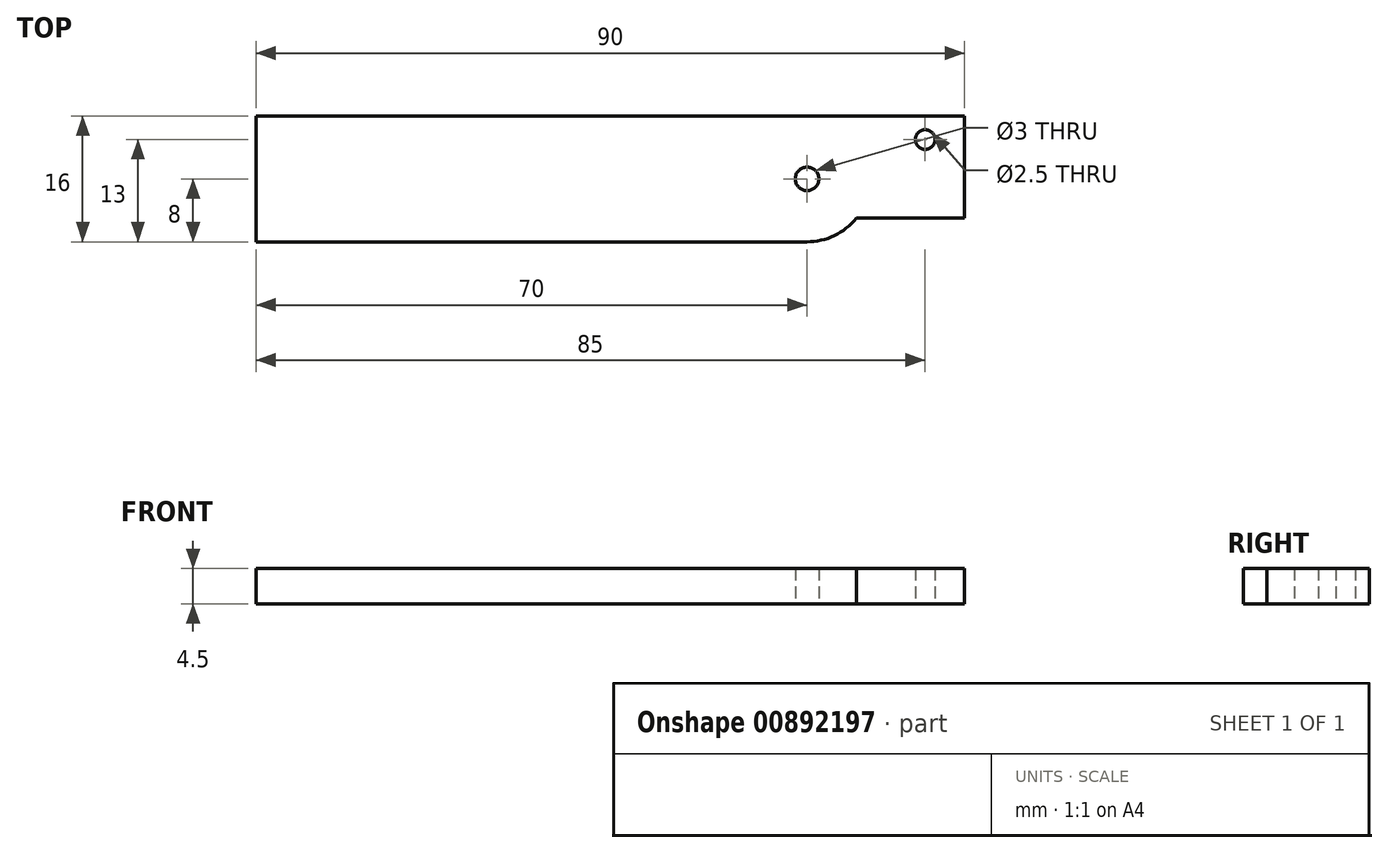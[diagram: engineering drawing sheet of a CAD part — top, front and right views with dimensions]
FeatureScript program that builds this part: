
annotation { "Feature Type Name" : "Feature", "Feature Type Description" : "" }
export const myFeature = defineFeature(function(context is Context, id is Id, definition is map)
    precondition{}
    {
        {
            var Q0;
            Q0=qCreatedBy(makeId("Top.planeOp"),FACE);
            var sketch = newSketch(context, id + "F0", { "sketchPlane" : qUnion([Q0])});
            skLineSegment(sketch, "E0.bottom", {"start": v(35, 8) * mm, "end": v(-35, 8) * mm});
            skLineSegment(sketch, "E0.top", {"start": v(35, -8) * mm, "end": v(-35, -8) * mm});
            skLineSegment(sketch, "E0.left", {"start": v(35, 8) * mm, "end": v(35, -8) * mm});
            skLineSegment(sketch, "E0.right", {"start": v(-35, 8) * mm, "end": v(-35, -8) * mm});
            skPoint(sketch, "E0.middle", {"position": v(0, 0) * mm});
            skArc(sketch, "E1", {"start": v(35, 8) * mm, "mid": v(43, 0) * mm, "end": v(35, -8) * mm});
            skPoint(sketch, "E2", {"position": v(35, -5) * mm});
            skLineSegment(sketch, "E3.bottom", {"start": v(35, -5) * mm, "end": v(55, -5) * mm});
            skLineSegment(sketch, "E3.top", {"start": v(35, 8) * mm, "end": v(55, 8) * mm});
            skLineSegment(sketch, "E3.left", {"start": v(35, -5) * mm, "end": v(35, 8) * mm});
            skLineSegment(sketch, "E3.right", {"start": v(55, -5) * mm, "end": v(55, 8) * mm});
            skPoint(sketch, "E4", {"position": v(50, 5) * mm});
            skSolve(sketch);
        }
        {
            var Q0;
            {var subQ4=sQuery(id+"F0.wireOp",EDGE,"E0.bottom");Q0=makeQuery(id+"F0.imprint","IMPRINT",FACE,{"disambiguationData":[TD([[makeQuery(id+"F0.imprint","IMPRINT",EDGE,{"derivedFrom":subQ4}),1.0]])]});}
            var Q1;
            {var subQ0=sQuery(id+"F0.wireOp",EDGE,"E1");var subQ3=sQuery(id+"F0.wireOp",EDGE,"E3.bottom");var subQ5=makeQuery(id+"F0.imprint","INTERSECT",VERTEX,{"derivedFrom":[subQ0,subQ3]});Q1=makeQuery(id+"F0.imprint","IMPRINT",FACE,{"disambiguationData":[TD([[makeQuery(id+"F0.imprint","IMPRINT",EDGE,{"disambiguationData":[TD([[subQ5,1.0]])],"derivedFrom":subQ3}),-1.0]])]});}
            var Q2;
            {var subQ0=sQuery(id+"F0.wireOp",EDGE,"E1");var subQ3=sQuery(id+"F0.wireOp",EDGE,"E3.bottom");var subQ5=makeQuery(id+"F0.imprint","INTERSECT",VERTEX,{"derivedFrom":[subQ0,subQ3]});Q2=makeQuery(id+"F0.imprint","IMPRINT",FACE,{"disambiguationData":[TD([[makeQuery(id+"F0.imprint","IMPRINT",EDGE,{"disambiguationData":[TD([[subQ5,1.0]])],"derivedFrom":subQ3}),1.0]])]});}
            var Q3;
            {var subQ0=sQuery(id+"F0.wireOp",EDGE,"E3.top");Q3=makeQuery(id+"F0.imprint","IMPRINT",FACE,{"disambiguationData":[TD([[makeQuery(id+"F0.imprint","IMPRINT",EDGE,{"derivedFrom":subQ0}),-1.0]])]});}
            extrude(context, id + "F1", {"entities" : qUnion([Q0, Q1, Q2, Q3]), "depth" : 4.5 * mm, "offsetDistance" : 25.4 * mm});
        }
        {
            var Q0;
            Q0=sQuery(id+"F0.wireOp",VERTEX,"E1.center");
            var Q1;
            Q1=makeQuery(id+"F1.opExtrude","SWEPT_BODY",BODY,{"disambiguationData":[OSD([sQuery(id+"F0.wireOp",EDGE,"E0.bottom"),sQuery(id+"F0.wireOp",EDGE,"E0.top"),sQuery(id+"F0.wireOp",EDGE,"E0.right"),sQuery(id+"F0.wireOp",EDGE,"E1"),sQuery(id+"F0.wireOp",EDGE,"E3.bottom"),sQuery(id+"F0.wireOp",EDGE,"E3.top"),sQuery(id+"F0.wireOp",EDGE,"E3.right")])]});
            hole(context, id + "F2", {"style" : HoleStyle.SIMPLE, "endStyle" : HoleEndStyle.BLIND, "oppositeDirection" : true, "holeDiameter" : 3 * mm, "majorDiameter" : 6.35 * mm, "holeDepth" : 10 * mm, "isTappedThrough" : true, "tappedDepth" : 12.7 * mm, "tapClearance" : 3, "locations" : qUnion([Q0]), "scope" : qUnion([Q1])});
        }
        {
            var Q0;
            Q0=sQuery(id+"F0.wireOp",VERTEX,"E4");
            var Q1;
            Q1=makeQuery(id+"F1.opExtrude","SWEPT_BODY",BODY,{"disambiguationData":[OSD([sQuery(id+"F0.wireOp",EDGE,"E0.bottom"),sQuery(id+"F0.wireOp",EDGE,"E0.top"),sQuery(id+"F0.wireOp",EDGE,"E0.right"),sQuery(id+"F0.wireOp",EDGE,"E1"),sQuery(id+"F0.wireOp",EDGE,"E3.bottom"),sQuery(id+"F0.wireOp",EDGE,"E3.top"),sQuery(id+"F0.wireOp",EDGE,"E3.right")])]});
            hole(context, id + "F3", {"style" : HoleStyle.SIMPLE, "endStyle" : HoleEndStyle.BLIND, "oppositeDirection" : true, "holeDiameter" : 2.5 * mm, "majorDiameter" : 6.35 * mm, "holeDepth" : 10 * mm, "isTappedThrough" : true, "tappedDepth" : 12.7 * mm, "tapClearance" : 3, "locations" : qUnion([Q0]), "scope" : qUnion([Q1])});
        }
    });
